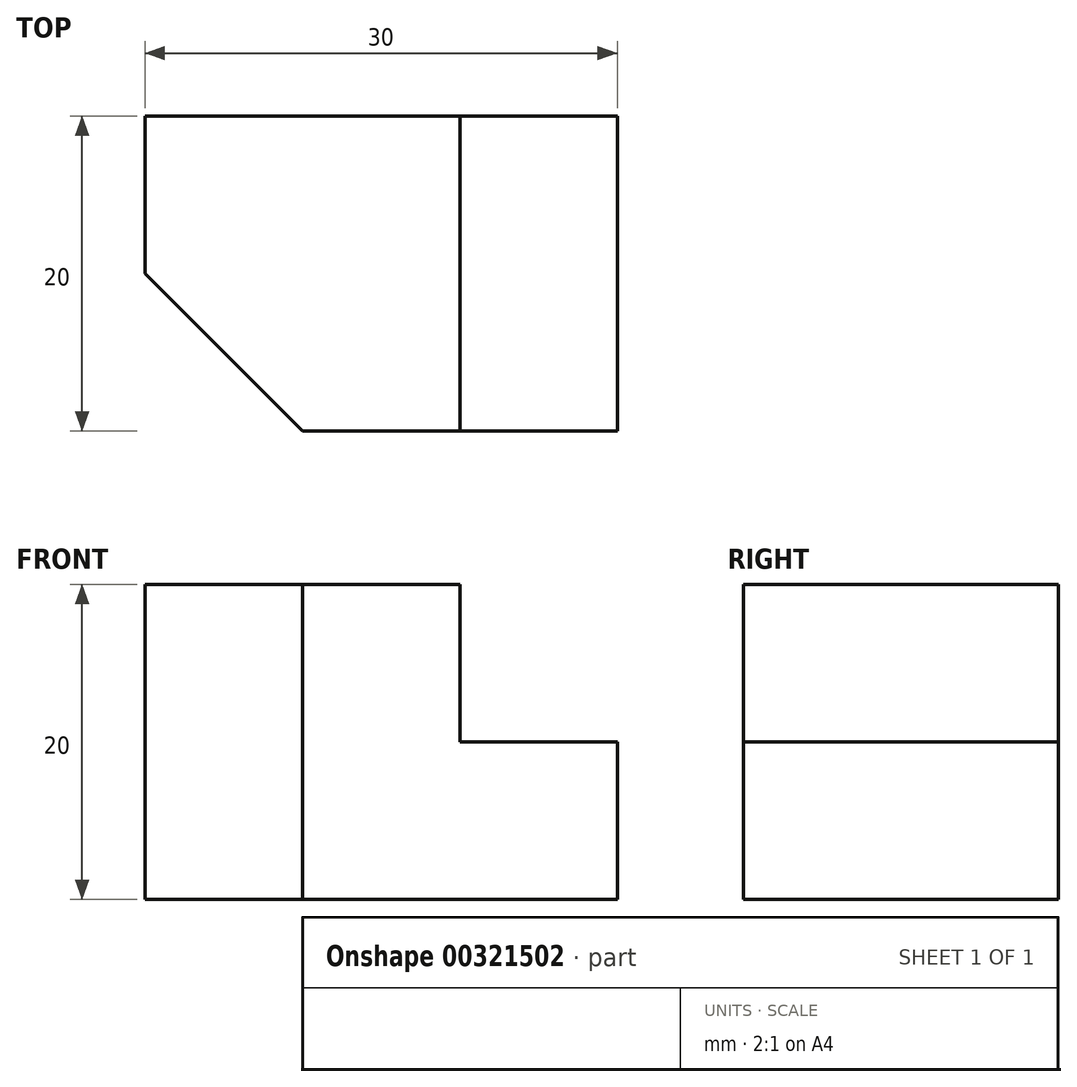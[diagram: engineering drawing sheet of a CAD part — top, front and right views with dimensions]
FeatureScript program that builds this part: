
annotation { "Feature Type Name" : "Feature", "Feature Type Description" : "" }
export const myFeature = defineFeature(function(context is Context, id is Id, definition is map)
    precondition{}
    {
        {
            var Q0;
            Q0=qCreatedBy(makeId("Top.planeOp"),FACE);
            var sketch = newSketch(context, id + "F0", { "sketchPlane" : qUnion([Q0])});
            skLineSegment(sketch, "E0.bottom", {"start": v(10, 0) * mm, "end": v(30, 0) * mm});
            skLineSegment(sketch, "E0.top", {"start": v(0, 20) * mm, "end": v(30, 20) * mm});
            skLineSegment(sketch, "E0.left", {"start": v(0, 10) * mm, "end": v(0, 20) * mm});
            skLineSegment(sketch, "E0.right", {"start": v(30, 0) * mm, "end": v(30, 20) * mm});
            skLineSegment(sketch, "E1", {"start": v(0, 10) * mm, "end": v(10, 0) * mm});
            skLineSegment(sketch, "E2", {"start": v(20, 20) * mm, "end": v(20, 0) * mm});
            skSolve(sketch);
        }
        {
            var Q0;
            Q0 = qSketchRegion(id + "F0", true);
            extrude(context, id + "F1", {"entities" : qUnion([Q0]), "depth" : 20 * mm});
        }
        {
            var Q0;
            Q0=makeQuery(id+"F1.opExtrude","CAP_FACE",FACE,{"disambiguationData":[OSD([sQuery(id+"F0.wireOp",EDGE,"E0.bottom"),sQuery(id+"F0.wireOp",EDGE,"E0.top"),sQuery(id+"F0.wireOp",EDGE,"E0.left"),sQuery(id+"F0.wireOp",EDGE,"E0.right"),sQuery(id+"F0.wireOp",EDGE,"E1")])],"isStart":false});
            var sketch = newSketch(context, id + "F2", { "sketchPlane" : qUnion([Q0])});
            skLineSegment(sketch, "E3.bottom", {"start": v(30, 20) * mm, "end": v(20, 20) * mm});
            skLineSegment(sketch, "E3.top", {"start": v(30, 0) * mm, "end": v(20, 0) * mm});
            skLineSegment(sketch, "E3.left", {"start": v(30, 20) * mm, "end": v(30, 0) * mm});
            skLineSegment(sketch, "E3.right", {"start": v(20, 20) * mm, "end": v(20, 0) * mm});
            skSolve(sketch);
        }
        {
            var Q0;
            Q0 = qSketchRegion(id + "F2", true);
            extrude(context, id + "F3", {"entities" : qUnion([Q0]), "operationType" : NewBodyOperationType.REMOVE, "oppositeDirection" : true, "depth" : 10 * mm});
        }
    });
